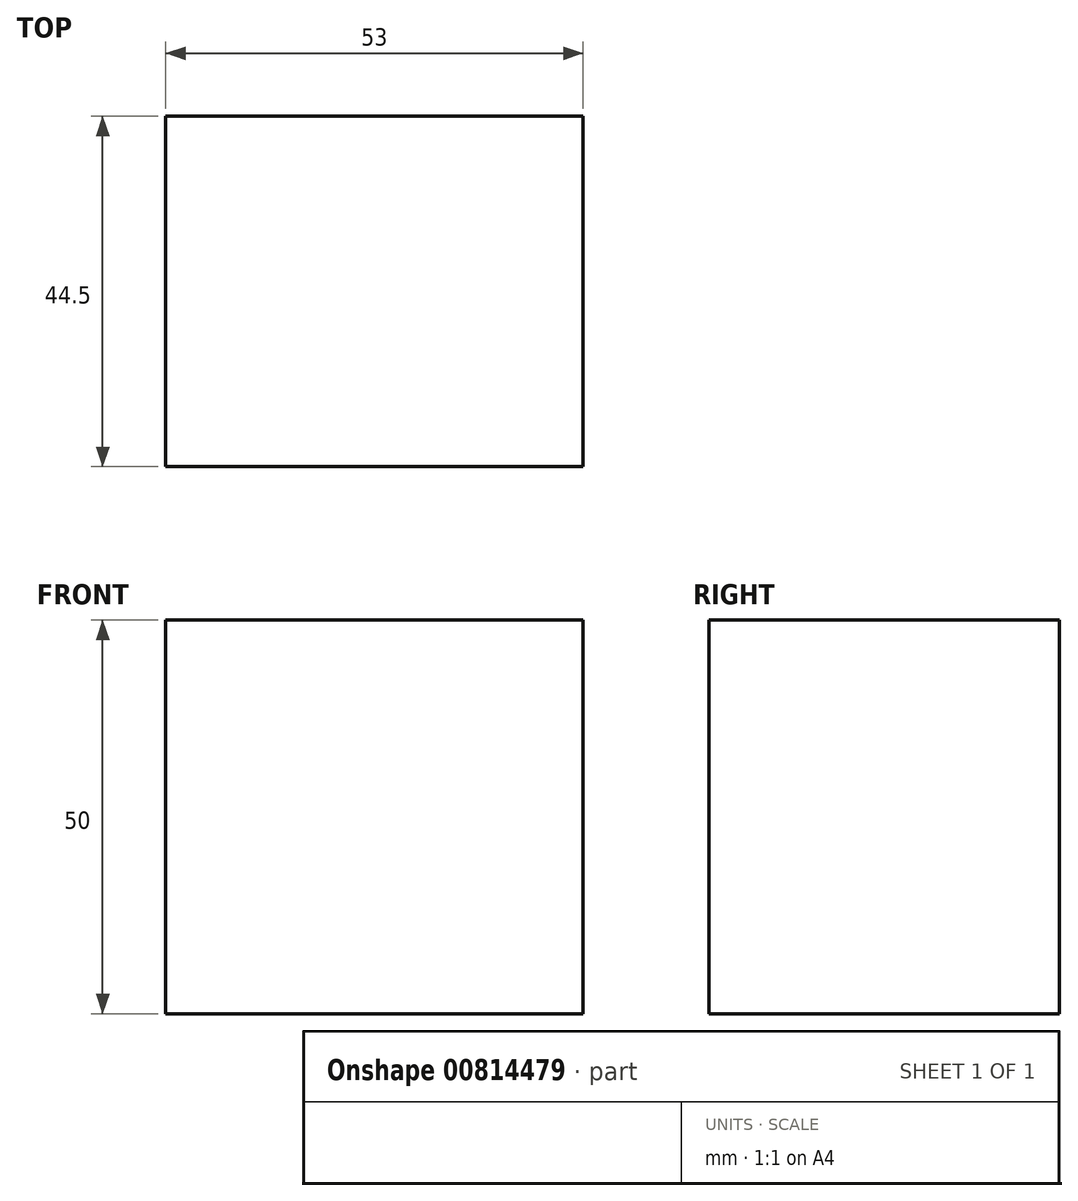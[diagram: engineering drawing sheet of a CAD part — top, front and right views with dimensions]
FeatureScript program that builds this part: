
annotation { "Feature Type Name" : "Feature", "Feature Type Description" : "" }
export const myFeature = defineFeature(function(context is Context, id is Id, definition is map)
    precondition{}
    {
        {
            var Q0;
            Q0=qCreatedBy(makeId("Front.planeOp"),FACE);
            var sketch = newSketch(context, id + "F0", { "sketchPlane" : qUnion([Q0])});
            skLineSegment(sketch, "E0.bottom", {"start": v(0, 0) * mm, "end": v(53, 0) * mm});
            skLineSegment(sketch, "E0.top", {"start": v(0, -50) * mm, "end": v(53, -50) * mm});
            skLineSegment(sketch, "E0.left", {"start": v(0, 0) * mm, "end": v(0, -50) * mm});
            skLineSegment(sketch, "E0.right", {"start": v(53, 0) * mm, "end": v(53, -50) * mm});
            skSolve(sketch);
        }
        {
            var Q0;
            Q0 = qSketchRegion(id + "F0", true);
            extrude(context, id + "F1", {"entities" : qUnion([Q0]), "depth" : 44.5 * mm, "offsetDistance" : 25 * mm});
        }
    });
